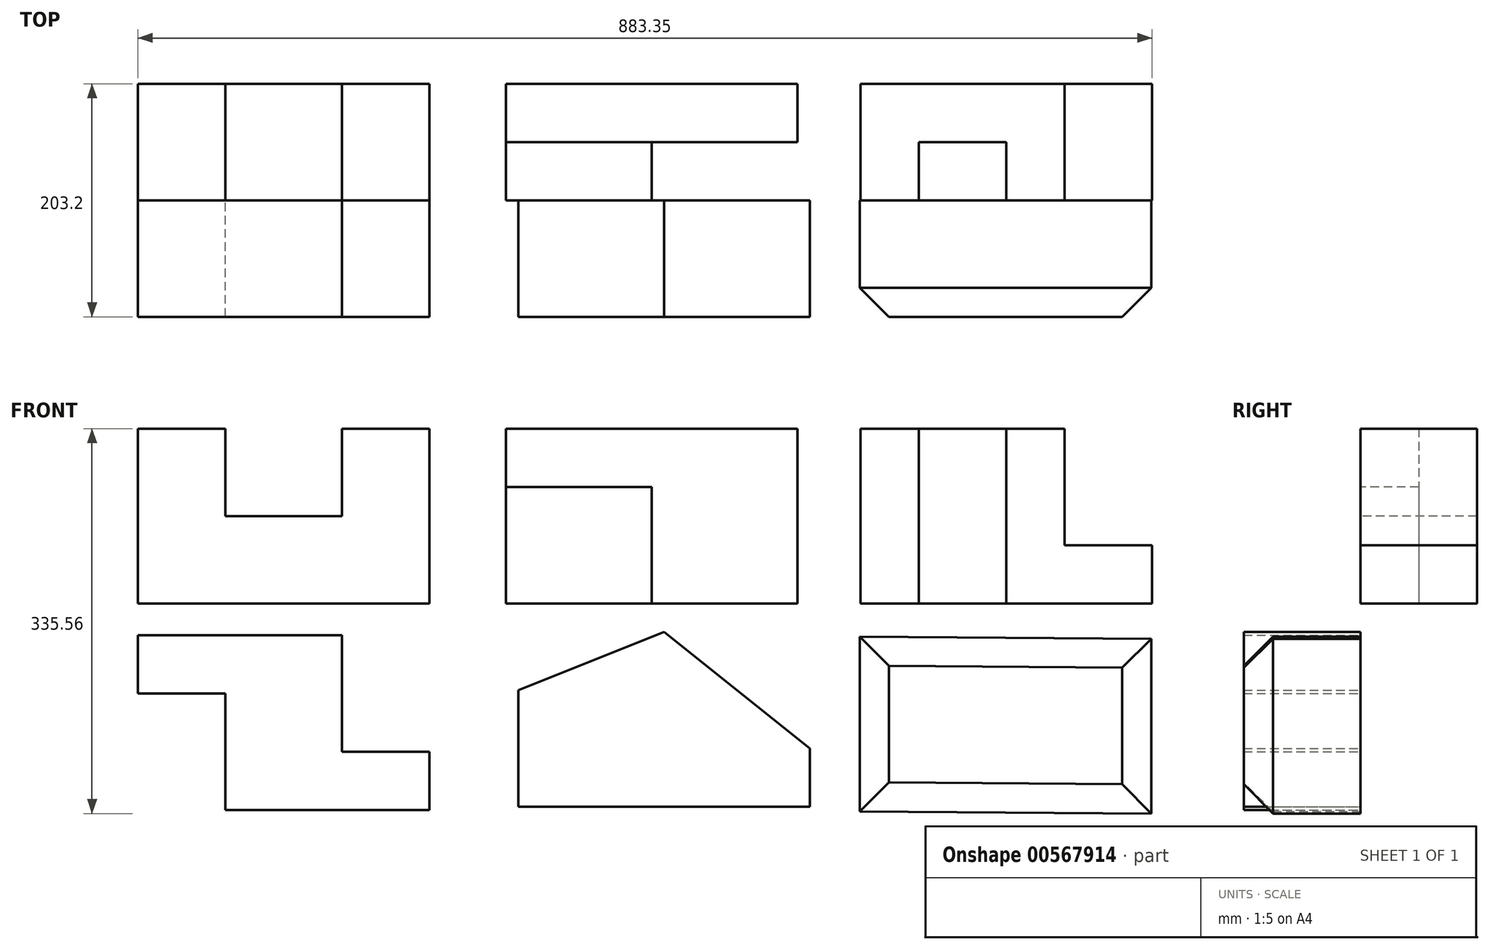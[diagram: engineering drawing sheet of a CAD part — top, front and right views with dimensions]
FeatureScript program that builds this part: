
annotation { "Feature Type Name" : "Feature", "Feature Type Description" : "" }
export const myFeature = defineFeature(function(context is Context, id is Id, definition is map)
    precondition{}
    {
        {
            var Q0;
            Q0=qCreatedBy(makeId("Front.planeOp"),FACE);
            var sketch = newSketch(context, id + "F0", { "sketchPlane" : qUnion([Q0])});
            skLineSegment(sketch, "E0", {"start": v(0, 0) * mm, "end": v(254, 0) * mm});
            skLineSegment(sketch, "E1", {"start": v(254, 0) * mm, "end": v(254, 152.4) * mm});
            skLineSegment(sketch, "E2", {"start": v(254, 152.4) * mm, "end": v(177.8, 152.4) * mm});
            skLineSegment(sketch, "E3", {"start": v(177.8, 152.4) * mm, "end": v(177.8, 76.2) * mm});
            skLineSegment(sketch, "E4", {"start": v(76.2, 76.2) * mm, "end": v(76.2, 152.4) * mm});
            skLineSegment(sketch, "E5", {"start": v(76.2, 152.4) * mm, "end": v(0, 152.4) * mm});
            skLineSegment(sketch, "E6", {"start": v(177.8, 76.2) * mm, "end": v(76.2, 76.2) * mm});
            skLineSegment(sketch, "E7", {"start": v(0, 0) * mm, "end": v(0, 152.4) * mm});
            skSolve(sketch);
        }
        {
            var Q0;
            Q0=makeQuery(id+"F0.imprint","IMPRINT",FACE,{"disambiguationData":[TD([[makeQuery(id+"F0.imprint","IMPRINT",EDGE,{"derivedFrom":sQuery(id+"F0.wireOp",EDGE,"E0")}),1.0]])]});
            extrude(context, id + "F1", {"entities" : qUnion([Q0]), "oppositeDirection" : true, "depth" : 101.6 * mm, "offsetDistance" : 25.4 * mm});
        }
        {
            var Q0;
            Q0=qCreatedBy(makeId("Top.planeOp"),FACE);
            var sketch = newSketch(context, id + "F2", { "sketchPlane" : qUnion([Q0])});
            skLineSegment(sketch, "E8", {"start": v(574.42, 101.6) * mm, "end": v(320.42, 101.6) * mm});
            skLineSegment(sketch, "E9", {"start": v(320.42, 101.6) * mm, "end": v(320.42, 0) * mm});
            skLineSegment(sketch, "E10", {"start": v(574.42, 101.6) * mm, "end": v(574.42, 50.8) * mm});
            skLineSegment(sketch, "E11", {"start": v(574.42, 50.8) * mm, "end": v(447.42, 50.8) * mm});
            skLineSegment(sketch, "E12", {"start": v(447.42, 50.8) * mm, "end": v(447.42, 0) * mm});
            skLineSegment(sketch, "E13", {"start": v(447.42, 0) * mm, "end": v(320.42, 0) * mm});
            skSolve(sketch);
        }
        {
            var Q0;
            Q0=makeQuery(id+"F2.imprint","IMPRINT",FACE,{"disambiguationData":[TD([[makeQuery(id+"F2.imprint","IMPRINT",EDGE,{"derivedFrom":sQuery(id+"F2.wireOp",EDGE,"E8")}),1.0]])]});
            extrude(context, id + "F3", {"entities" : qUnion([Q0]), "depth" : 152.4 * mm, "offsetDistance" : 25.4 * mm});
        }
        {
            var Q0;
            Q0=makeQuery(id+"F3.opExtrude","SWEPT_FACE",FACE,{"disambiguationData":[OSD([sQuery(id+"F2.wireOp",EDGE,"E13")])]});
            var sketch = newSketch(context, id + "F4", { "sketchPlane" : qUnion([Q0])});
            skLineSegment(sketch, "E14.bottom", {"start": v(320.42, 152.4) * mm, "end": v(447.42, 152.4) * mm});
            skLineSegment(sketch, "E14.top", {"start": v(320.42, 101.6) * mm, "end": v(447.42, 101.6) * mm});
            skLineSegment(sketch, "E14.left", {"start": v(320.42, 152.4) * mm, "end": v(320.42, 101.6) * mm});
            skLineSegment(sketch, "E14.right", {"start": v(447.42, 152.4) * mm, "end": v(447.42, 101.6) * mm});
            skSolve(sketch);
        }
        {
            var Q0;
            Q0=makeQuery(id+"F4.imprint","IMPRINT",FACE,{"disambiguationData":[TD([[makeQuery(id+"F4.imprint","IMPRINT",EDGE,{"derivedFrom":sQuery(id+"F4.wireOp",EDGE,"E14.bottom")}),1.0]])]});
            extrude(context, id + "F5", {"entities" : qUnion([Q0]), "operationType" : NewBodyOperationType.REMOVE, "oppositeDirection" : true, "depth" : 50.8 * mm, "offsetDistance" : 25.4 * mm});
        }
        {
            var Q0;
            Q0=qCreatedBy(makeId("Front.planeOp"),FACE);
            var sketch = newSketch(context, id + "F6", { "sketchPlane" : qUnion([Q0])});
            skLineSegment(sketch, "E15", {"start": v(629.35, 0) * mm, "end": v(883.35, 0) * mm});
            skLineSegment(sketch, "E16", {"start": v(629.35, 152.4) * mm, "end": v(629.35, 0) * mm});
            skLineSegment(sketch, "E17", {"start": v(883.35, 0) * mm, "end": v(883.35, 50.8) * mm});
            skLineSegment(sketch, "E18", {"start": v(883.35, 50.8) * mm, "end": v(807.15, 50.8) * mm});
            skLineSegment(sketch, "E19", {"start": v(807.15, 50.8) * mm, "end": v(807.15, 152.4) * mm});
            skLineSegment(sketch, "E20", {"start": v(807.15, 152.4) * mm, "end": v(629.35, 152.4) * mm});
            skSolve(sketch);
        }
        {
            var Q0;
            Q0 = qSketchRegion(id + "F6", true);
            extrude(context, id + "F7", {"entities" : qUnion([Q0]), "oppositeDirection" : true, "depth" : 101.6 * mm, "offsetDistance" : 25.4 * mm});
        }
        {
            var Q0;
            Q0=makeQuery(id+"F7.opExtrude","SWEPT_FACE",FACE,{"disambiguationData":[OSD([sQuery(id+"F6.wireOp",EDGE,"E20")])]});
            var sketch = newSketch(context, id + "F8", { "sketchPlane" : qUnion([Q0])});
            skLineSegment(sketch, "E21.bottom", {"start": v(680.15, 0) * mm, "end": v(756.35, 0) * mm});
            skLineSegment(sketch, "E21.top", {"start": v(680.15, 50.8) * mm, "end": v(756.35, 50.8) * mm});
            skLineSegment(sketch, "E21.left", {"start": v(680.15, 0) * mm, "end": v(680.15, 50.8) * mm});
            skLineSegment(sketch, "E21.right", {"start": v(756.35, 0) * mm, "end": v(756.35, 50.8) * mm});
            skSolve(sketch);
        }
        {
            var Q0;
            Q0 = qSketchRegion(id + "F8", true);
            extrude(context, id + "F9", {"entities" : qUnion([Q0]), "operationType" : NewBodyOperationType.REMOVE, "oppositeDirection" : true, "depth" : 152.4 * mm, "offsetDistance" : 25.4 * mm});
        }
        {
            var Q0;
            Q0=qCreatedBy(makeId("Front.planeOp"),FACE);
            var sketch = newSketch(context, id + "F10", { "sketchPlane" : qUnion([Q0])});
            skLineSegment(sketch, "E22", {"start": v(0, -27.68) * mm, "end": v(0, -78.48) * mm});
            skLineSegment(sketch, "E23", {"start": v(0, -78.48) * mm, "end": v(76.2, -78.48) * mm});
            skLineSegment(sketch, "E24", {"start": v(76.2, -78.48) * mm, "end": v(76.2, -180.08) * mm});
            skLineSegment(sketch, "E25", {"start": v(76.2, -180.08) * mm, "end": v(254, -180.08) * mm});
            skLineSegment(sketch, "E26", {"start": v(254, -180.08) * mm, "end": v(254, -129.28) * mm});
            skLineSegment(sketch, "E27", {"start": v(254, -129.28) * mm, "end": v(177.8, -129.28) * mm});
            skLineSegment(sketch, "E28", {"start": v(177.8, -129.28) * mm, "end": v(177.8, -27.68) * mm});
            skLineSegment(sketch, "E29", {"start": v(0, -27.68) * mm, "end": v(177.8, -27.68) * mm});
            skSolve(sketch);
        }
        {
            var Q0;
            Q0=makeQuery(id+"F10.imprint","IMPRINT",FACE,{"disambiguationData":[TD([[makeQuery(id+"F10.imprint","IMPRINT",EDGE,{"derivedFrom":sQuery(id+"F10.wireOp",EDGE,"E22")}),1.0]])]});
            extrude(context, id + "F11", {"entities" : qUnion([Q0]), "depth" : 101.6 * mm, "offsetDistance" : 25.4 * mm});
        }
        {
            var Q0;
            Q0=qCreatedBy(makeId("Front.planeOp"),FACE);
            var sketch = newSketch(context, id + "F12", { "sketchPlane" : qUnion([Q0])});
            skLineSegment(sketch, "E30", {"start": v(585.24, -177.28) * mm, "end": v(331.24, -177.28) * mm});
            skLineSegment(sketch, "E31", {"start": v(331.24, -177.28) * mm, "end": v(331.24, -75.68) * mm});
            skLineSegment(sketch, "E32", {"start": v(585.24, -177.28) * mm, "end": v(585.24, -126.48) * mm});
            skPoint(sketch, "E33.startSnap0", {"position": v(458.24, -177.28) * mm});
            skLineSegment(sketch, "E34", {"start": v(331.24, -75.68) * mm, "end": v(458.24, -24.88) * mm});
            skLineSegment(sketch, "E35", {"start": v(585.24, -126.48) * mm, "end": v(458.24, -24.88) * mm});
            skSolve(sketch);
        }
        {
            var Q0;
            Q0 = qSketchRegion(id + "F12", true);
            extrude(context, id + "F13", {"entities" : qUnion([Q0]), "depth" : 101.6 * mm, "offsetDistance" : 25.4 * mm});
        }
        {
            var Q0;
            Q0=qCreatedBy(makeId("Front.planeOp"),FACE);
            var sketch = newSketch(context, id + "F14", { "sketchPlane" : qUnion([Q0])});
            skLineSegment(sketch, "E36", {"start": v(628.8, -181.3) * mm, "end": v(628.8, -28.9) * mm});
            skLineSegment(sketch, "E37", {"start": v(628.8, -28.9) * mm, "end": v(882.8, -30.76) * mm});
            skLineSegment(sketch, "E38", {"start": v(882.8, -30.76) * mm, "end": v(882.8, -183.16) * mm});
            skLineSegment(sketch, "E39", {"start": v(882.8, -183.16) * mm, "end": v(628.8, -181.3) * mm});
            skSolve(sketch);
        }
        {
            var Q0;
            Q0=makeQuery(id+"F14.imprint","IMPRINT",FACE,{"disambiguationData":[TD([[makeQuery(id+"F14.imprint","IMPRINT",EDGE,{"derivedFrom":sQuery(id+"F14.wireOp",EDGE,"E36")}),-1.0]])]});
            extrude(context, id + "F15", {"entities" : qUnion([Q0]), "depth" : 101.6 * mm, "offsetDistance" : 25.4 * mm});
        }
        {
            var Q0;
            Q0=makeQuery(id+"F15.opExtrude","CAP_EDGE",EDGE,{"disambiguationData":[OSD([sQuery(id+"F14.wireOp",EDGE,"E37")])],"isStart":false});
            var Q1;
            Q1=makeQuery(id+"F15.opExtrude","CAP_EDGE",EDGE,{"disambiguationData":[OSD([sQuery(id+"F14.wireOp",EDGE,"E38")])],"isStart":false});
            var Q2;
            Q2=makeQuery(id+"F15.opExtrude","CAP_EDGE",EDGE,{"disambiguationData":[OSD([sQuery(id+"F14.wireOp",EDGE,"E36")])],"isStart":false});
            chamfer(context, id + "F16", {"entities" : qUnion([Q0, Q1, Q2]), "width" : 25.4 * mm, "tangentPropagation" : true});
        }
        {
            var Q0;
            Q0=makeQuery(id+"F15.opExtrude","CAP_EDGE",EDGE,{"disambiguationData":[OSD([sQuery(id+"F14.wireOp",EDGE,"E39")])],"isStart":false});
            chamfer(context, id + "F17", {"entities" : qUnion([Q0]), "width" : 25.4 * mm, "tangentPropagation" : true});
        }
    });
